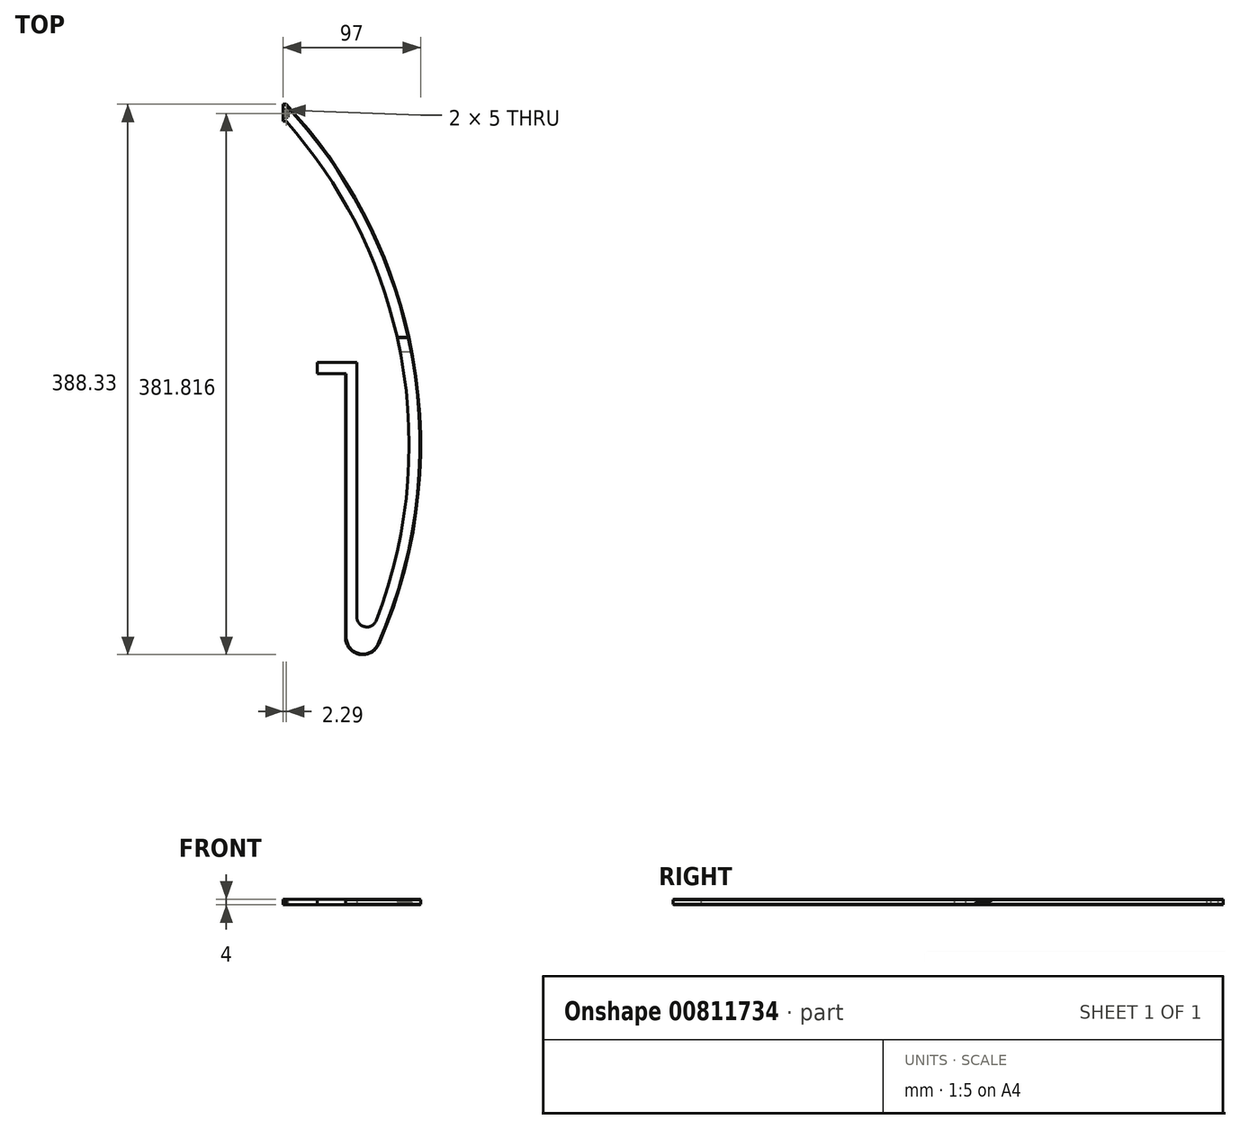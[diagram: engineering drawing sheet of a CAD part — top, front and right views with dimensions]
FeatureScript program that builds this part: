
annotation { "Feature Type Name" : "Feature", "Feature Type Description" : "" }
export const myFeature = defineFeature(function(context is Context, id is Id, definition is map)
    precondition{}
    {
        {
            var Q0;
            Q0=qCreatedBy(makeId("Top.planeOp"),FACE);
            var sketch = newSketch(context, id + "F0", { "sketchPlane" : qUnion([Q0])});
            skLineSegment(sketch, "E0.bottom", {"start": v(0, 130) * mm, "end": v(1, 130) * mm, "construction": true});
            skLineSegment(sketch, "E0.top", {"start": v(0, 0) * mm, "end": v(1, 0) * mm, "construction": true});
            skLineSegment(sketch, "E0.left", {"start": v(0, 130) * mm, "end": v(0, 0) * mm, "construction": true});
            skLineSegment(sketch, "E0.right", {"start": v(1, 130) * mm, "end": v(1, 0) * mm, "construction": true});
            skLineSegment(sketch, "E1.MirrorCS", {"start": v(0, 130) * mm, "end": v(-1, 130) * mm, "construction": true});
            skLineSegment(sketch, "E2.MirrorCS", {"start": v(0, 0) * mm, "end": v(-1, 0) * mm, "construction": true});
            skLineSegment(sketch, "E3.MirrorCS", {"start": v(-1, 130) * mm, "end": v(-1, 0) * mm, "construction": true});
            skLineSegment(sketch, "E4.bottom", {"start": v(-27, 0) * mm, "end": v(27, 0) * mm, "construction": true});
            skLineSegment(sketch, "E4.top", {"start": v(-27, -60) * mm, "end": v(27, -60) * mm, "construction": true});
            skLineSegment(sketch, "E4.left", {"start": v(-27, 0) * mm, "end": v(-27, -60) * mm, "construction": true});
            skLineSegment(sketch, "E4.right", {"start": v(27, 0) * mm, "end": v(27, -60) * mm, "construction": true});
            skPoint(sketch, "E5", {"position": v(0, 0) * mm});
            skFitSpline(sketch, "E6", {"points": [v(-3.65, -60) * mm, v(-26.1, -90.7) * mm, v(-30.1, -114.33) * mm, v(-25.29, -133.16) * mm, v(-4.46, -141.98) * mm, v(0, -141.98) * mm], "startDerivative": vector(-54.33, -120.02) * mm, "endDerivative": vector(34.86, 4.53) * mm, "construction": true});
            skFitSpline(sketch, "E7.MirrorCS", {"points": [v(3.65, -60) * mm, v(26.1, -90.7) * mm, v(30.1, -114.33) * mm, v(25.29, -133.16) * mm, v(4.46, -141.98) * mm, v(0, -141.98) * mm], "startDerivative": vector(54.33, -120.02) * mm, "endDerivative": vector(-34.86, 4.53) * mm, "construction": true});
            skLineSegment(sketch, "E8.top", {"start": v(-5, 118) * mm, "end": v(5, 118) * mm, "construction": true});
            skLineSegment(sketch, "E8.left", {"start": v(-5, 130) * mm, "end": v(-5, 118) * mm, "construction": true});
            skPoint(sketch, "E9", {"position": v(0, 118) * mm});
            skLineSegment(sketch, "E10", {"start": v(5, 130) * mm, "end": v(5, 130) * mm});
            skLineSegment(sketch, "E11", {"start": v(70.46, -240) * mm, "end": v(273.03, -240) * mm, "construction": true});
            skLineSegment(sketch, "E12", {"start": v(100, 228.83) * mm, "end": v(100, -265.28) * mm, "construction": true});
            skLineSegment(sketch, "E13", {"start": v(27, -60) * mm, "end": v(27, -52) * mm});
            skLineSegment(sketch, "E14", {"start": v(27, -52) * mm, "end": v(55, -52) * mm});
            skLineSegment(sketch, "E15", {"start": v(55, -52) * mm, "end": v(55, -231.73) * mm});
            skLineSegment(sketch, "E16", {"start": v(27, -60) * mm, "end": v(47, -60) * mm});
            skLineSegment(sketch, "E17", {"start": v(47, -60) * mm, "end": v(47, -246.08) * mm});
            skArc(sketch, "E18", {"start": v(47, -246.08) * mm, "mid": v(56.73, -258.07) * mm, "end": v(70.46, -251) * mm});
            skArc(sketch, "E19", {"start": v(70.46, -251) * mm, "mid": v(94.93, -50.67) * mm, "end": v(5, 130) * mm});
            skArc(sketch, "E20", {"start": v(55, -231.73) * mm, "mid": v(60.75, -238.66) * mm, "end": v(68.6, -234.28) * mm});
            skArc(sketch, "E21", {"start": v(68.6, -234.28) * mm, "mid": v(86.45, -49.18) * mm, "end": v(5, 118) * mm});
            skLineSegment(sketch, "E22", {"start": v(70.46, -251) * mm, "end": v(59.3, -276.44) * mm, "construction": true});
            skLineSegment(sketch, "E23", {"start": v(68.6, -234.28) * mm, "end": v(51.03, -279.5) * mm, "construction": true});
            skLineSegment(sketch, "E24", {"start": v(29.08, -251) * mm, "end": v(187.18, -251) * mm, "construction": true});
            skLineSegment(sketch, "E25", {"start": v(5, 130) * mm, "end": v(3, 130) * mm});
            skLineSegment(sketch, "E26", {"start": v(3, 130) * mm, "end": v(3, 118) * mm});
            skLineSegment(sketch, "E27", {"start": v(3, 118) * mm, "end": v(5, 118) * mm});
            skLineSegment(sketch, "E28", {"start": v(-5, 130) * mm, "end": v(5, 130) * mm, "construction": true});
            skLineSegment(sketch, "E29.bottom", {"start": v(4.3, 125.99) * mm, "end": v(6.3, 125.99) * mm});
            skLineSegment(sketch, "E29.top", {"start": v(4.3, 120.99) * mm, "end": v(6.3, 120.99) * mm});
            skLineSegment(sketch, "E29.left", {"start": v(4.3, 125.99) * mm, "end": v(4.3, 120.99) * mm});
            skLineSegment(sketch, "E29.right", {"start": v(6.3, 125.99) * mm, "end": v(6.3, 120.99) * mm});
            skLineSegment(sketch, "E30", {"start": v(70.46, -251) * mm, "end": v(65.5, -206.3) * mm, "construction": true});
            skSolve(sketch);
        }
        {
            var Q0;
            Q0 = qSketchRegion(id + "F0", true);
            extrude(context, id + "F1", {"entities" : qUnion([Q0]), "depth" : 4 * mm, "offsetDistance" : 25 * mm});
        }
        {
            var Q0;
            Q0=makeQuery(id+"F1.opExtrude","CAP_EDGE",EDGE,{"disambiguationData":[OSD([sQuery(id+"F0.wireOp",EDGE,"E19")])],"isStart":true});
            var Q1;
            Q1=makeQuery(id+"F1.opExtrude","CAP_EDGE",EDGE,{"disambiguationData":[OSD([sQuery(id+"F0.wireOp",EDGE,"E19")])],"isStart":false});
            chamfer(context, id + "F2", {"entities" : qUnion([Q0, Q1]), "width" : 0.5 * mm, "tangentPropagation" : true});
        }
        {
            var Q0;
            Q0=qCreatedBy(makeId("Right.planeOp"),FACE);
            var sketch = newSketch(context, id + "F3", { "sketchPlane" : qUnion([Q0])});
            skLineSegment(sketch, "E31", {"start": v(-44.85, 0) * mm, "end": v(-44.85, 2.08) * mm});
            skLineSegment(sketch, "E32", {"start": v(-44.85, 2.08) * mm, "end": v(-34.52, 2.08) * mm});
            skLineSegment(sketch, "E33", {"start": v(-34.52, 2.08) * mm, "end": v(-34.52, 4) * mm});
            skLineSegment(sketch, "E34", {"start": v(-34.52, 4) * mm, "end": v(-34.37, 4) * mm});
            skLineSegment(sketch, "E35", {"start": v(-34.37, 4) * mm, "end": v(-34.37, 1.93) * mm});
            skLineSegment(sketch, "E36", {"start": v(-34.37, 1.93) * mm, "end": v(-44.7, 1.93) * mm});
            skLineSegment(sketch, "E37", {"start": v(-44.7, 1.93) * mm, "end": v(-44.7, 0) * mm});
            skLineSegment(sketch, "E38", {"start": v(-44.7, 0) * mm, "end": v(-44.85, 0) * mm});
            skSolve(sketch);
        }
        {
            var Q0;
            Q0 = qSketchRegion(id + "F3", true);
            extrude(context, id + "F4", {"entities" : qUnion([Q0]), "operationType" : NewBodyOperationType.REMOVE, "depth" : 150 * mm, "offsetDistance" : 25 * mm});
        }
    });
